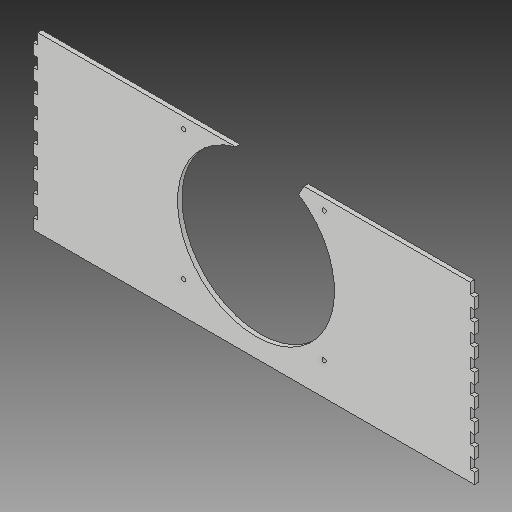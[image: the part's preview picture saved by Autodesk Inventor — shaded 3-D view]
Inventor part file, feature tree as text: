
AUTODESK INVENTOR PART (.ipt)
format: ipt  version: 2019 (Build 230136000, 136)  size: 211,968 bytes
history: native  units: mm
features: reference x15, other x4, extrude x4, sketch x4
ambient origin geometry x8: Origin, YZ Plane, XZ Plane, XY Plane, X Axis, Y Axis, Z Axis, Center Point
bodies: Body1 (feature_tree)
feature tree (27):
  other  "Твердое тело1"
  extrude  "Выдавливание1"  Depth=140.0mm
  extrude  "Выдавливание2"  Depth=400.0mm
  extrude  "Выдавливание3"  Depth=150.0mm
  extrude  "Выдавливание4"  Depth=125.0mm
  sketch  "Эскиз1"
  reference  "Ссылка1"
  reference  "Ссылка2"
  reference  "Ссылка3"
  reference  "Ссылка4"
  reference  "Ссылка5"
  reference  "Ссылка6"
  reference  "Ссылка7"
  reference  "Ссылка8"
  reference  "Ссылка9"
  reference  "Ссылка10"
  sketch  "Эскиз2"
  reference  "Ссылка11"
  sketch  "Эскиз3"
  sketch  "Эскиз4"
  reference  "Ссылка12"
  reference  "Ссылка13"
  reference  "Ссылка14"
  reference  "Ссылка15"
  parser-record x1  (decoder bookkeeping rows leaked as tree rows — omitted from the tree; the rows remain in map.json)
  other  "kowsh.iam"
  other  "mot37:1"
note: 1 file-system path scrubbed to <path> (originals preserved in map.json)
